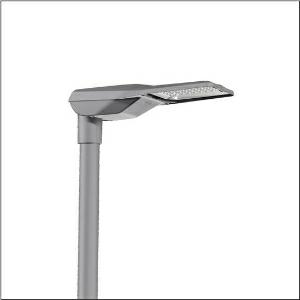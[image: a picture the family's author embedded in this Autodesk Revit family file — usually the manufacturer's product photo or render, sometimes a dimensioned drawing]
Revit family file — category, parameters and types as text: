
# Revit family: streetlight_sl_21_iq_mini___st0_5a_5xe2b41d08hb_2494
name_source: partatom
category: Lighting Fixtures
units: mm (PartAtom-declared; Revit-internal decimal feet)

## family parameters
Cut with Voids When Loaded = No
Host = Face
Light Source = No
Part Type = Normal
Room Calculation Point = No
Round Connector Dimension = Use Diameter
Shared = No

## types (1)
- --- (1 x LED, 9860 lm, 70.9 W, 4000K)
    Apparent Load = 71 VA
    CIE Flux Codes = 41 75 97 100 100
    Color Rendering = 70
    Color Temperature = 4000K
    Default Elevation = 1800 mm
    Description = Streetlight SL 21 mini, mast luminaire, primary light control with lens, of PMMA, primary optical cover: cover, of toughened safety glass, transparent, light distribution: ST0.5a, light emission: direct distribution, primary light characteristic: asymmetric, installation type: post-top, side-entry, LED, High Power LED, rated luminous flux: 9.860lm, luminous efficacy: 139lm/W, light colour: 740, colour temperature: 4000K, control gear: ECG iQ, control: Auto-Match, Temp-Guard, Lumen-Switch, Night-Set, Smart-Wire, Light-Fading, Desk-Remote (wireless, voltage-free reading and setting of iQ features in the workshop via application-optimized NFC function/RFID function), optimised constant luminous flux control (CLO 2.0), mains connection: 220..240V, AC, 50/60Hz, start of lifetime: 71W, end of lifetime: 75W, reduction: 31W, luminaire housing, of diecast aluminium, powder-coated, Siteco® metallic grey (DB 702S), corrosivity category C5 according to DIN EN ISO 12944, length: 628mm, width: 235mm, height: 110mm, spigot size: 60/76mm (post-top) and 42/60/76mm (side-entry), mast flange for spigot size: 42mm: 5XC10008XM4, 60mm: 5XC10008XM2, 76/60mm: 5XC10108XM1, protection rating (complete): IP66, insulation class (complete): insulation class II (safety insulation), certification: CE, ENEC, VDE, impact resistance: IK09, permissible operating ambient temperature for outdoor applications: -40..+50°C, standard-compliant lighting for roads and squares, packaging unit: 1 piece

Light Distribution: ST0.5a
    Height = 110 mm
    Lamp = 1 x LED
    Lamp Light Flux = 9860 lm
    Lamp Power = 70.9 W
    Lamp count = 1
    Length = 625 mm
    Luminous efficacy = 139 lm/W
    Manufacturer = Siteco
    ModVariant = No
    Model = 5XE2B41D08HB
    Number of Poles = 1
    OnlyDefault = Yes
    Power Factor = 1
    Product Name = Streetlight SL 21 iQ mini | ST0.5a
    Product group = mast luminaire | pylon top
    ProductGroupID = 6100
    Protection Class = Protection class II
    Protection Degree = IP 66
    RLX_Detail_Level = 1
    RlxData = <blob elided: 103021 chars, md5=4d3dcfa9>
    Socket = socket
    Standby Power = 0 W
    System Light Flux = 9860 lm
    System Power = 71 W
    Type Comments = factory setting: luminous flux: 100 % | dim-lin: 254 | 711 mA
    Type Image = l_1003519.jpg
    URL = http://relux.com
    VarID = @adj_069797
    Voltage = 0 V
    Weight = 0.00 kg
    Width = 234 mm

## geometry (parser evidence)
native form markers: Blend x4, Sweep x11
no freeform markers — native parametric forms only
